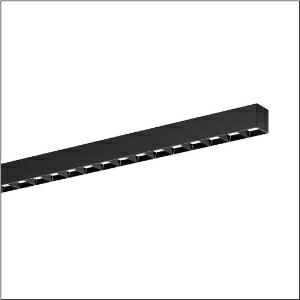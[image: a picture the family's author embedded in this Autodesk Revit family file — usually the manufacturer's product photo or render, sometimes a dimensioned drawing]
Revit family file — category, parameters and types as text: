
# Revit family: silica_r__21_51mx22tat4b_b010
name_source: partatom
category: Lighting Fixtures
units: mm (PartAtom-declared; Revit-internal decimal feet)

## family parameters
Cut with Voids When Loaded = No
Host = Face
Light Source = No
Part Type = Normal
Room Calculation Point = No
Round Connector Dimension = Use Diameter
Shared = No

## types (1)
- --- (1 x LED, 3720 lm, 32.1 W, 6500K)
    Apparent Load = 32 VA
    CIE Flux Codes = 84 100 100 100 100
    Color Rendering = 80
    Color Temperature = 6500K
    Default Elevation = 1800 mm
    Description = Silica® 21, office luminaire, primary light control with darklight reflector, of PMMA, black, CAT 2 (L<= 3000cd/m²), light emission: direct distribution, primary light characteristic: symmetric, installation type: surface-mounted, LED, rated luminous flux: 3.720lm, luminous efficacy: 110lm/W, light colour: 8tw, colour temperature: 2700..6500K, control gear: ECG DALI, with terminal, 3+2-pole, max. 2.5mm², mains connection: 220..240V, AC, 50/60Hz, rated input power: 33.8W, luminaire housing, of aluminium, jet black (RAL 9005), length: 1.204mm, width: 53mm, height: 53mm, protection rating (complete): IP20, insulation class (complete): insulation class I (protective earthing), certification: CE, permissible operating ambient temperature: 0..+35°C, standard: EN 50419, packaging unit: 1 piece
    Height = 0 mm  [stored 0 ft]
    Lamp = 1 x LED
    Lamp Light Flux = 3720 lm
    Lamp Power = 32.1 W
    Lamp count = 1
    Length = 1204 mm
    Luminous efficacy = 116 lm/W
    Manufacturer = Siteco
    ModVariant = No
    Model = 51MX22TAT4B
    Mounting Place = Ceiling
    Mounting Type = Recessed
    Number of Poles = 1
    OnlyDefault = Yes
    Power Factor = 1
    Product Name = Silica® 21
    Product group = office luminaire | ceiling recessed
    ProductGroupID = 401
    Protection Class = Protection class I
    Protection Degree = IP 20
    RLX_Detail_Level = 1
    RLX_Emergency_Light_Flux = 0 lm
    RLX_Emergency_Type = 0
    RLX_Emergency_Type_DB = No
    RlxData = <blob elided: 40245 chars, md5=54a06d31>
    Socket = socket
    Standby Power = 0 W
    System Light Flux = 3720 lm
    System Power = 32 W
    Type Comments = individual setting
    Type Image = l_1313577.jpg
    URL = http://relux.com
    VarID = @adj_089511
    Voltage = 0 V
    Weight = 0.00 kg
    Width = 53 mm

note: [stored X ft] marks values corroborated as IEEE doubles in the binary element streams (Revit-internal decimal feet)

## geometry (parser evidence)
native form markers: Blend x4, Sweep x11
no freeform markers — native parametric forms only
